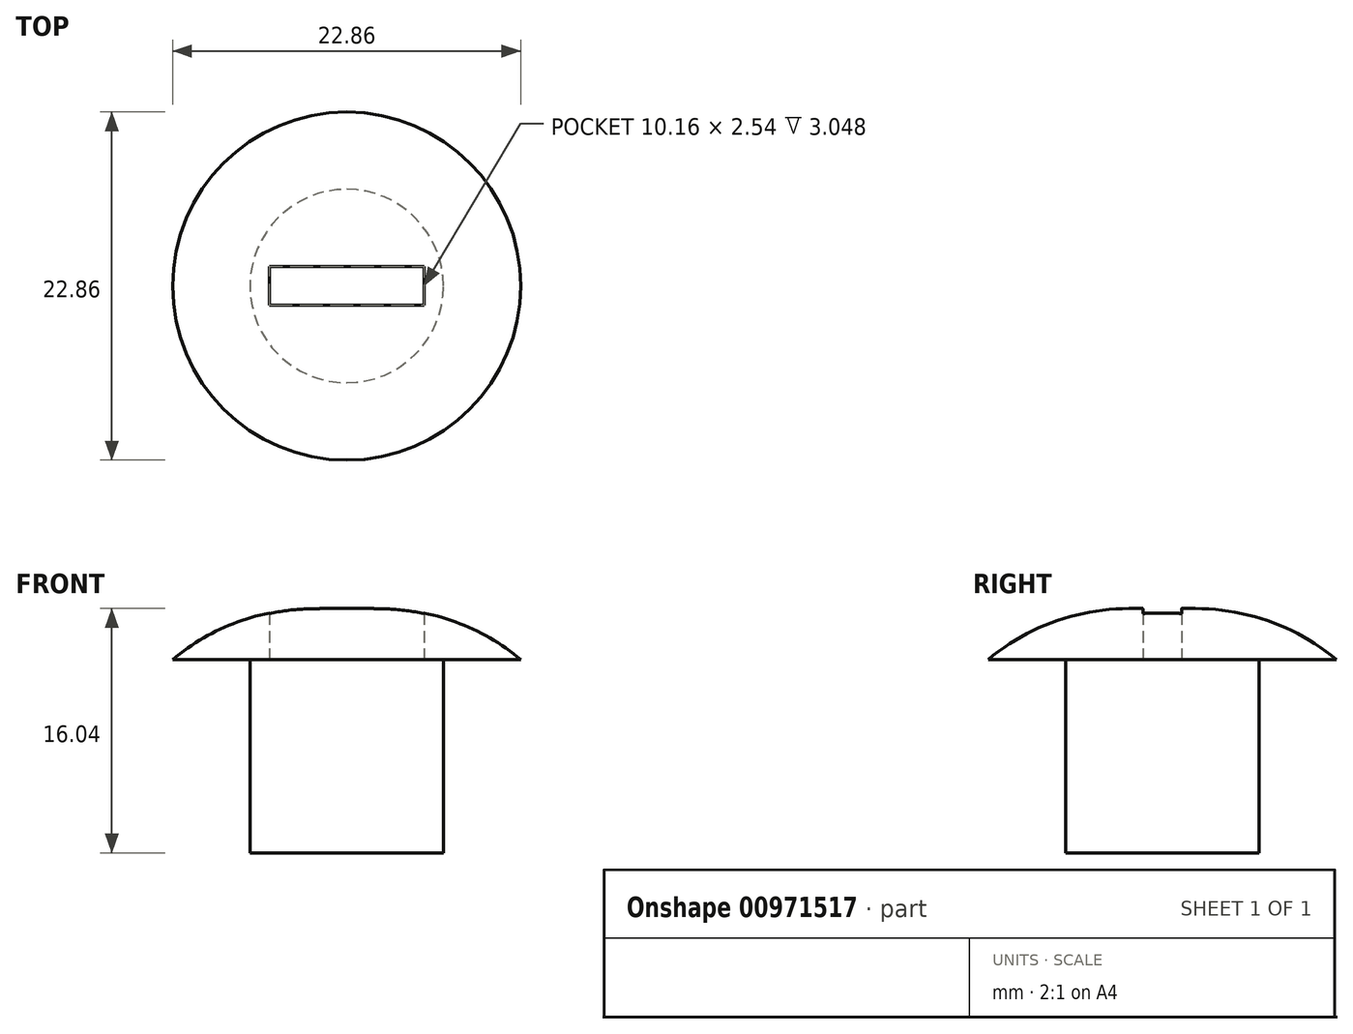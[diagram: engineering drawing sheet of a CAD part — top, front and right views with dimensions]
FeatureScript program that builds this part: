
annotation { "Feature Type Name" : "Feature", "Feature Type Description" : "" }
export const myFeature = defineFeature(function(context is Context, id is Id, definition is map)
    precondition{}
    {
        {
            var Q0;
            Q0=qCreatedBy(makeId("Front.planeOp"),FACE);
            var sketch = newSketch(context, id + "F0", { "sketchPlane" : qUnion([Q0])});
            skLineSegment(sketch, "E0", {"start": v(0, 0) * mm, "end": v(0, 15.88) * mm});
            skArc(sketch, "E1", {"start": v(11.43, 12.7) * mm, "mid": v(6.06, 15.51) * mm, "end": v(0, 15.88) * mm});
            skLineSegment(sketch, "E2", {"start": v(11.43, 12.7) * mm, "end": v(6.35, 12.7) * mm});
            skLineSegment(sketch, "E3", {"start": v(6.35, 12.7) * mm, "end": v(6.35, 0) * mm});
            skLineSegment(sketch, "E4", {"start": v(6.35, 0) * mm, "end": v(0, 0) * mm});
            skLineSegment(sketch, "E5", {"start": v(0, 15.88) * mm, "end": v(0, -7.29) * mm, "construction": true});
            skSolve(sketch);
        }
        {
            var Q0;
            Q0 = qSketchRegion(id + "F0", true);
            var Q1;
            Q1=sQuery(id+"F0.wireOp",EDGE,"E5");
            revolve(context, id + "F1", {"surfaceOperationType" : NewSurfaceOperationType.NEW, "entities" : qUnion([Q0]), "axis" : qUnion([Q1]), "revolveType" : RevolveType.FULL});
        }
        {
            var Q0;
            Q0=makeQuery(id+"F1.opRevolve","SWEPT_FACE",FACE,{"disambiguationData":[OSD([sQuery(id+"F0.wireOp",EDGE,"E2")])]});
            var sketch = newSketch(context, id + "F2", { "sketchPlane" : qUnion([Q0])});
            skLineSegment(sketch, "E6.bottom", {"start": v(-5.08, -1.27) * mm, "end": v(5.08, -1.27) * mm});
            skLineSegment(sketch, "E6.top", {"start": v(-5.08, 1.27) * mm, "end": v(5.08, 1.27) * mm});
            skLineSegment(sketch, "E6.left", {"start": v(-5.08, -1.27) * mm, "end": v(-5.08, 1.27) * mm});
            skLineSegment(sketch, "E6.right", {"start": v(5.08, -1.27) * mm, "end": v(5.08, 1.27) * mm});
            skPoint(sketch, "E6.middle", {"position": v(0, 0) * mm});
            skSolve(sketch);
        }
        {
            var Q0;
            Q0 = qSketchRegion(id + "F2", true);
            extrude(context, id + "F3", {"entities" : qUnion([Q0]), "operationType" : NewBodyOperationType.REMOVE, "oppositeDirection" : true, "depth" : 25.4 * mm, "offsetDistance" : 25.4 * mm});
        }
    });
